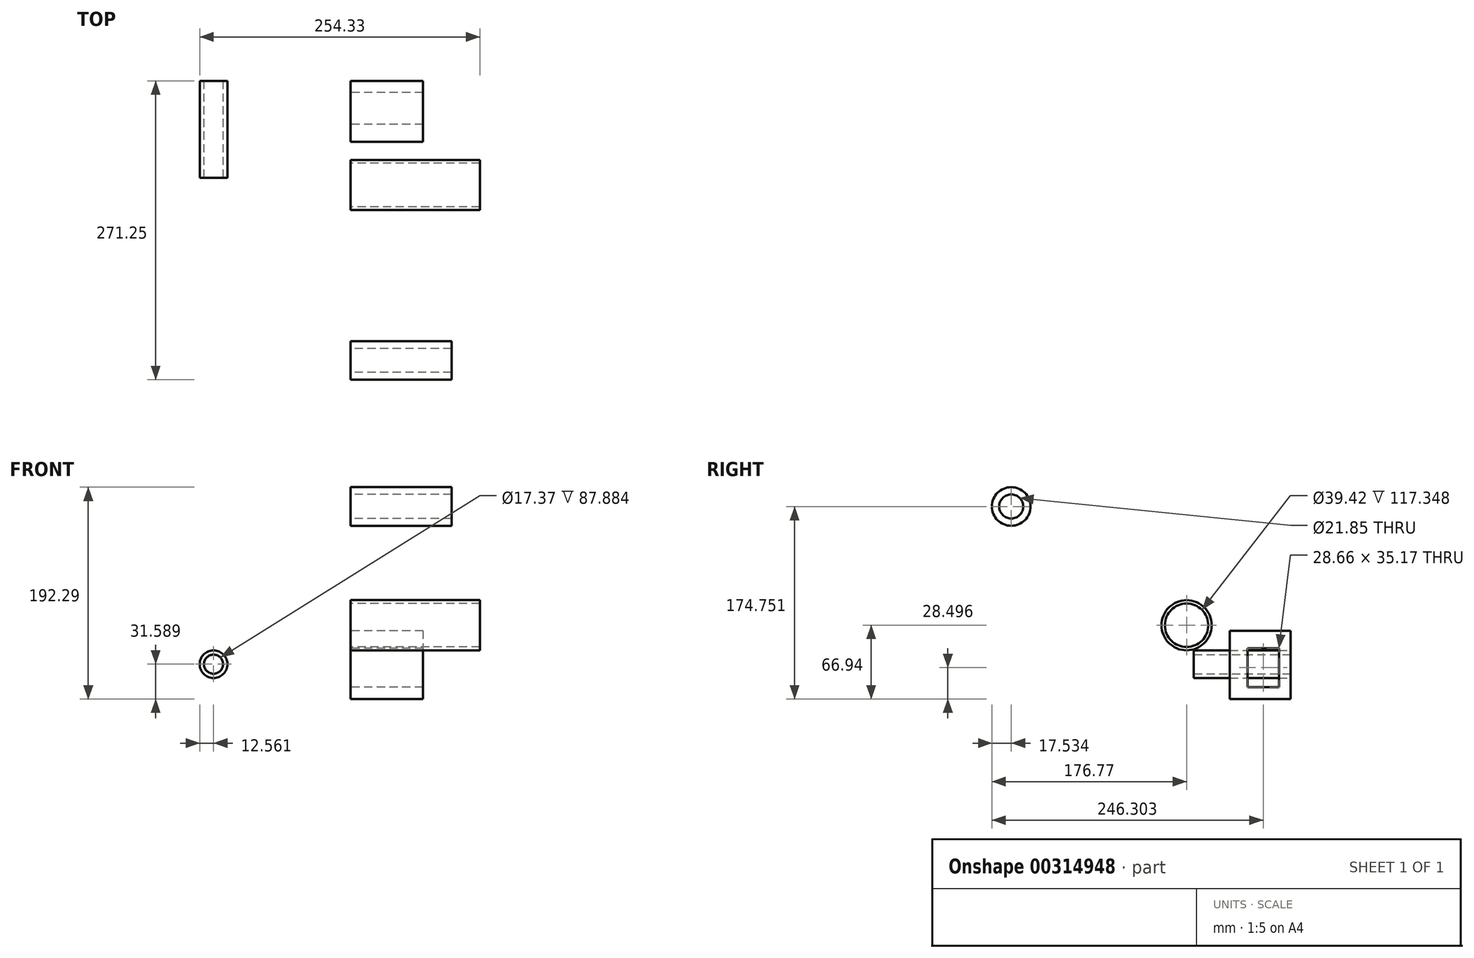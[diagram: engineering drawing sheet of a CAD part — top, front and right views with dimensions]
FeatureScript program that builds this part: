
annotation { "Feature Type Name" : "Feature", "Feature Type Description" : "" }
export const myFeature = defineFeature(function(context is Context, id is Id, definition is map)
    precondition{}
    {
        {
            var Q0;
            Q0=qCreatedBy(makeId("Front.planeOp"),FACE);
            var sketch = newSketch(context, id + "F0", { "sketchPlane" : qUnion([Q0])});
            skCircle(sketch, "E0", {"center": v(-124.42, 7.29) * mm, "radius": 12.56 * mm});
            skCircle(sketch, "E1", {"center": v(-124.42, 7.29) * mm, "radius": 8.68 * mm});
            skSolve(sketch);
        }
        {
            var Q0;
            Q0 = qSketchRegion(id + "F0", true);
            extrude(context, id + "F1", {"entities" : qUnion([Q0]), "depth" : 87.88 * mm});
        }
        {
            var Q0;
            Q0=qCreatedBy(makeId("Right.planeOp"),FACE);
            var sketch = newSketch(context, id + "F2", { "sketchPlane" : qUnion([Q0])});
            skCircle(sketch, "E2", {"center": v(-253.72, 150.45) * mm, "radius": 10.92 * mm});
            skCircle(sketch, "E3", {"center": v(-253.72, 150.45) * mm, "radius": 17.54 * mm});
            skSolve(sketch);
        }
        {
            var Q0;
            Q0 = qSketchRegion(id + "F2", true);
            extrude(context, id + "F3", {"entities" : qUnion([Q0]), "depth" : 91.7 * mm});
        }
        {
            var Q0;
            Q0=qCreatedBy(makeId("Right.planeOp"),FACE);
            var sketch = newSketch(context, id + "F4", { "sketchPlane" : qUnion([Q0])});
            skCircle(sketch, "E4", {"center": v(-94.48, 42.64) * mm, "radius": 19.71 * mm});
            skCircle(sketch, "E5", {"center": v(-94.48, 42.64) * mm, "radius": 22.76 * mm});
            skSolve(sketch);
        }
        {
            var Q0;
            Q0 = qSketchRegion(id + "F4", true);
            extrude(context, id + "F5", {"entities" : qUnion([Q0]), "depth" : 117.35 * mm});
        }
        {
            var Q0;
            Q0=qCreatedBy(makeId("Right.planeOp"),FACE);
            var sketch = newSketch(context, id + "F6", { "sketchPlane" : qUnion([Q0])});
            skLineSegment(sketch, "E6.bottom", {"start": v(-55.2, 37.71) * mm, "end": v(0, 37.71) * mm});
            skLineSegment(sketch, "E6.top", {"start": v(-55.2, -24.3) * mm, "end": v(0, -24.3) * mm});
            skLineSegment(sketch, "E6.left", {"start": v(-55.2, 37.71) * mm, "end": v(-55.2, -24.3) * mm});
            skLineSegment(sketch, "E6.right", {"start": v(0, 37.71) * mm, "end": v(0, -24.3) * mm});
            skLineSegment(sketch, "E7.bottom", {"start": v(-39.28, 21.78) * mm, "end": v(-10.62, 21.78) * mm});
            skLineSegment(sketch, "E7.top", {"start": v(-39.28, -13.39) * mm, "end": v(-10.62, -13.39) * mm});
            skLineSegment(sketch, "E7.left", {"start": v(-39.28, 21.78) * mm, "end": v(-39.28, -13.39) * mm});
            skLineSegment(sketch, "E7.right", {"start": v(-10.62, 21.78) * mm, "end": v(-10.62, -13.39) * mm});
            skSolve(sketch);
        }
        {
            var Q0;
            Q0 = qSketchRegion(id + "F6", true);
            extrude(context, id + "F7", {"entities" : qUnion([Q0]), "depth" : 65.8 * mm});
        }
    });
